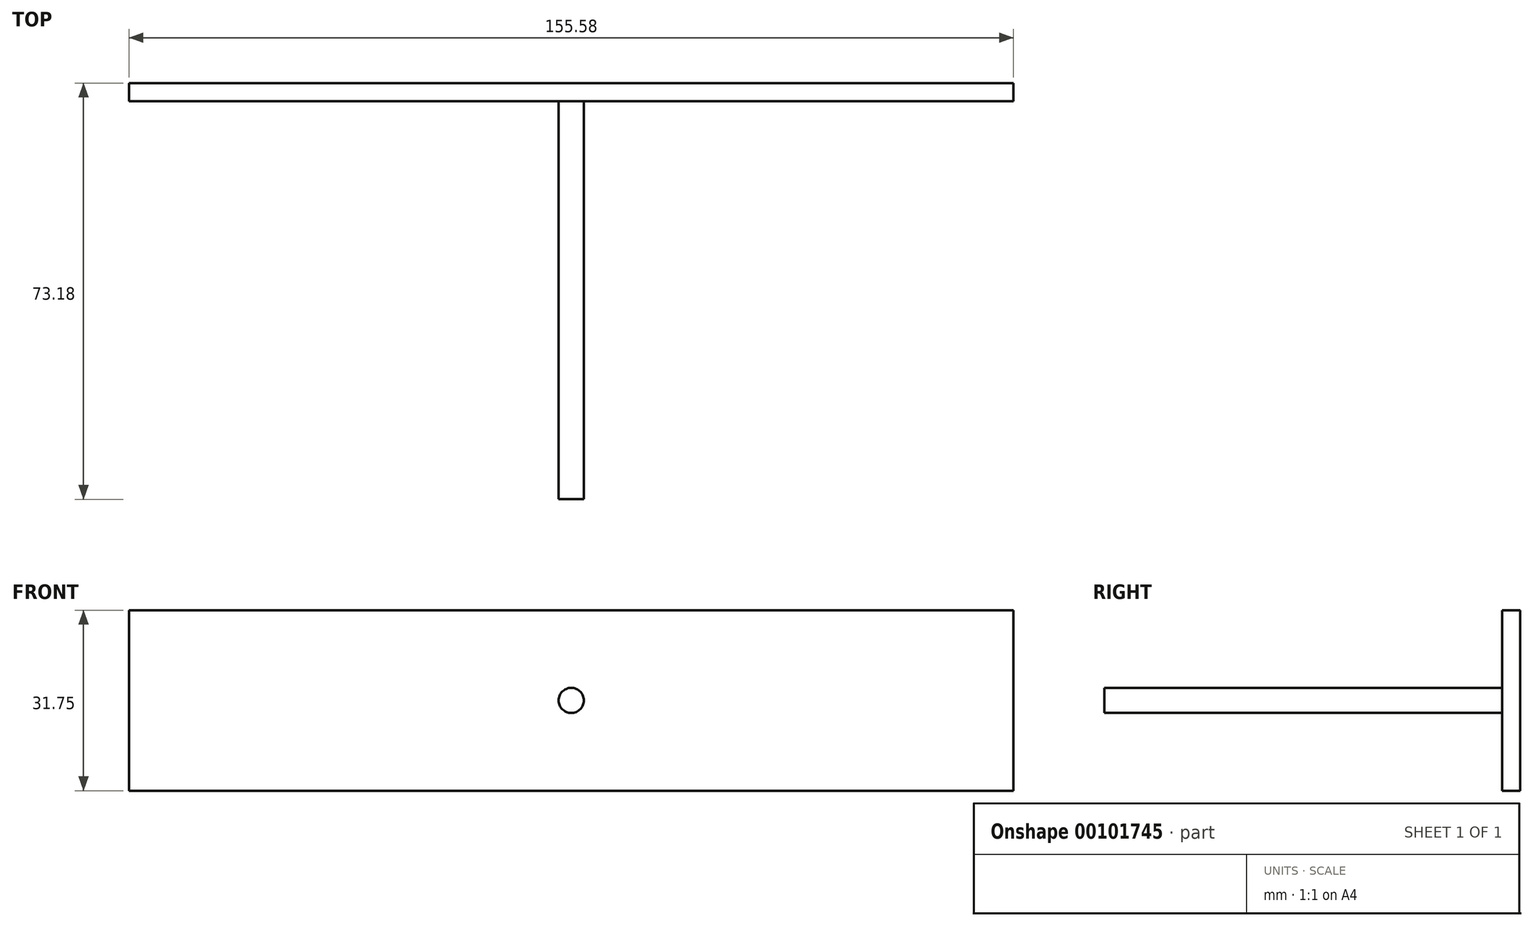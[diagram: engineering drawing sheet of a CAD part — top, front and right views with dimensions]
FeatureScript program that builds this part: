
annotation { "Feature Type Name" : "Feature", "Feature Type Description" : "" }
export const myFeature = defineFeature(function(context is Context, id is Id, definition is map)
    precondition{}
    {
        {
            var Q0;
            Q0=qCreatedBy(makeId("Front.planeOp"),FACE);
            var sketch = newSketch(context, id + "F0", { "sketchPlane" : qUnion([Q0])});
            skLineSegment(sketch, "E0.bottom", {"start": v(-39.18, 47.82) * mm, "end": v(116.4, 47.82) * mm});
            skLineSegment(sketch, "E0.top", {"start": v(-39.18, 16.07) * mm, "end": v(116.4, 16.07) * mm});
            skLineSegment(sketch, "E0.left", {"start": v(-39.18, 47.82) * mm, "end": v(-39.18, 16.07) * mm});
            skLineSegment(sketch, "E0.right", {"start": v(116.4, 47.82) * mm, "end": v(116.4, 16.07) * mm});
            skPoint(sketch, "E1", {"position": v(38.61, 47.82) * mm});
            skPoint(sketch, "E2", {"position": v(38.61, 16.07) * mm});
            skPoint(sketch, "E3", {"position": v(-39.18, 31.94) * mm});
            skPoint(sketch, "E4", {"position": v(116.4, 31.94) * mm});
            skLineSegment(sketch, "E5", {"start": v(38.61, 47.82) * mm, "end": v(38.61, 16.07) * mm});
            skPoint(sketch, "E6", {"position": v(38.61, 31.94) * mm});
            skSolve(sketch);
        }
        {
            var Q0;
            Q0=qSketchRegion(id+"F0",true);
            extrude(context, id + "F1", {"entities" : qUnion([Q0]), "depth" : 3.17 * mm});
        }
        {
            var Q0;
            Q0=makeQuery(id+"F1.opExtrude","CAP_FACE",FACE,{"disambiguationData":[OSD([sQuery(id+"F0.wireOp",EDGE,"E0.bottom"),sQuery(id+"F0.wireOp",EDGE,"E0.top"),sQuery(id+"F0.wireOp",EDGE,"E0.left"),sQuery(id+"F0.wireOp",EDGE,"E0.right")])],"isStart":false});
            var sketch = newSketch(context, id + "F2", { "sketchPlane" : qUnion([Q0])});
            skSolve(sketch);
        }
        {
            var Q0;
            Q0=makeQuery(id+"F2.imprint","IMPRINT",FACE,{"disambiguationData":[TD([[makeQuery(id+"F2.imprint","IMPRINT",EDGE,{"derivedFrom":makeQuery(id+"F1.opExtrude","CAP_EDGE",EDGE,{"disambiguationData":[OSD([sQuery(id+"F0.wireOp",EDGE,"E0.bottom")])],"isStart":false})}),-1.0]])]});
            var sketch = newSketch(context, id + "F3", { "sketchPlane" : qUnion([Q0])});
            skCircle(sketch, "E7", {"center": v(38.61, 31.95) * mm, "radius": 2.2 * mm});
            skSolve(sketch);
        }
        {
            var Q0;
            Q0=qSketchRegion(id+"F3",true);
            extrude(context, id + "F4", {"entities" : qUnion([Q0]), "operationType" : NewBodyOperationType.ADD, "depth" : 70 * mm});
        }
    });
